# Revit family: 38336
name_source: partatom
category: Plumbing Fixtures
units: mm (PartAtom-declared; Revit-internal decimal feet)

## family parameters
Always vertical = Yes
Cut with Voids When Loaded = No
Maintain Annotation Orientation = No
OmniClass Number = 23.45.00.00
OmniClass Title = Sanitary, Laundry, and Cleaning Equipment
Part Type = Normal
Room Calculation Point = No
Round Connector Dimension = Use Diameter
Shared = No
Work Plane-Based = Yes

## types (1)
- 38336-PRESTO
    - Hydraulic supply = 15.00 mm
    > Thermal resistance : = 75.0000 (m²·K)/W
    Default Elevation = 1219 mm
    Description = Self-Closing urinal valves
    Manufacturer = PRESTO
    Model = 38336
    RANGE = Self-Closing urinal valves
    Recommended pressure = 3.0 bar
    URL = https://www.prestodatashare.com
    brand = LES ROBINETS PRESTO
    flow = 5.0 L/min
    flow time = 6.0 s
    material = stainless steel vandal proof front, brushed finish
    min pressure = 1.0 bar
    pressure = 5.0 bar
    ref = 38336 - PRESTO 120 B

## geometry (parser evidence)
native form markers: Sweep x2
no freeform markers — native parametric forms only
